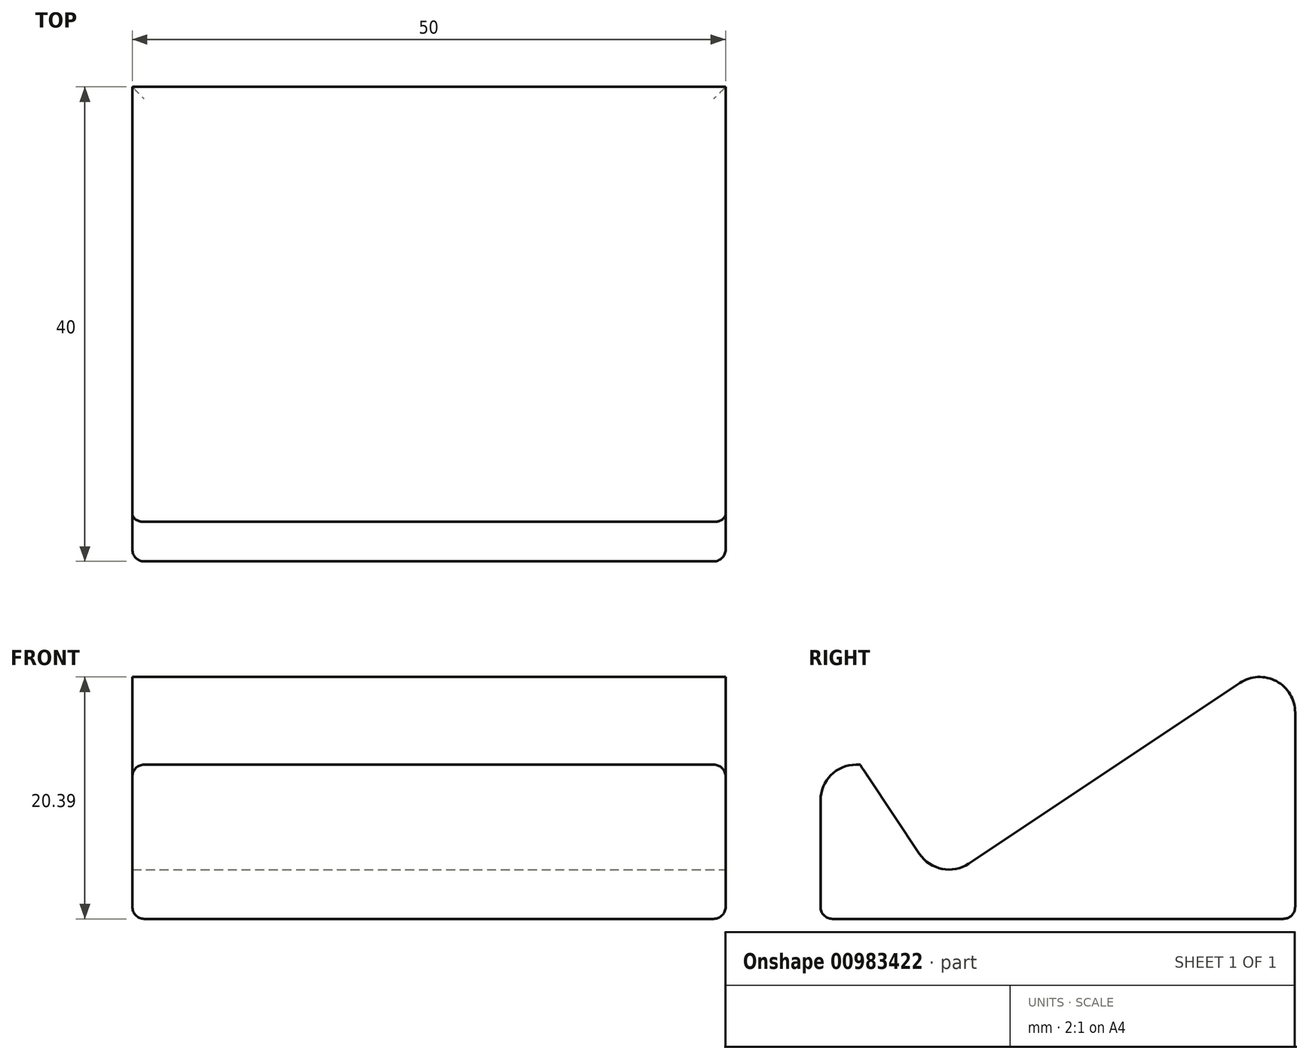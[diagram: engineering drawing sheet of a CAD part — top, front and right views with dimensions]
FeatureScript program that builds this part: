
annotation { "Feature Type Name" : "Feature", "Feature Type Description" : "" }
export const myFeature = defineFeature(function(context is Context, id is Id, definition is map)
    precondition{}
    {
        {
            var Q0;
            Q0=qCreatedBy(makeId("Top.planeOp"),FACE);
            var sketch = newSketch(context, id + "F0", { "sketchPlane" : qUnion([Q0])});
            skLineSegment(sketch, "E0.bottom", {"start": v(25, -20) * mm, "end": v(-25, -20) * mm});
            skLineSegment(sketch, "E0.top", {"start": v(25, 20) * mm, "end": v(-25, 20) * mm});
            skLineSegment(sketch, "E0.left", {"start": v(25, -20) * mm, "end": v(25, 20) * mm});
            skLineSegment(sketch, "E0.right", {"start": v(-25, -20) * mm, "end": v(-25, 20) * mm});
            skPoint(sketch, "E0.middle", {"position": v(0, 0) * mm});
            skSolve(sketch);
        }
        {
            var Q0;
            Q0=makeQuery(id+"F0.imprint","IMPRINT",FACE,{"disambiguationData":[TD([[makeQuery(id+"F0.imprint","IMPRINT",EDGE,{"derivedFrom":sQuery(id+"F0.wireOp",EDGE,"E0.bottom")}),-1.0]])]});
            extrude(context, id + "F1", {"entities" : qUnion([Q0]), "depth" : 3 * mm, "offsetDistance" : 25 * mm});
        }
        {
            var Q0;
            Q0=makeQuery(id+"F1.opExtrude","CAP_FACE",FACE,{"disambiguationData":[OSD([sQuery(id+"F0.wireOp",EDGE,"E0.bottom"),sQuery(id+"F0.wireOp",EDGE,"E0.top"),sQuery(id+"F0.wireOp",EDGE,"E0.left"),sQuery(id+"F0.wireOp",EDGE,"E0.right")])],"isStart":false});
            var sketch = newSketch(context, id + "F2", { "sketchPlane" : qUnion([Q0])});
            skLineSegment(sketch, "E1.bottom", {"start": v(-25, -20) * mm, "end": v(25, -20) * mm});
            skLineSegment(sketch, "E1.top", {"start": v(-25, -10) * mm, "end": v(25, -10) * mm});
            skLineSegment(sketch, "E1.left", {"start": v(-25, -20) * mm, "end": v(-25, -10) * mm});
            skLineSegment(sketch, "E1.right", {"start": v(25, -20) * mm, "end": v(25, -10) * mm});
            skSolve(sketch);
        }
        {
            var Q0;
            {var subQ0=sQuery(id+"F2.wireOp",EDGE,"E1.top");Q0=makeQuery(id+"F2.imprint","IMPRINT",FACE,{"disambiguationData":[TD([[makeQuery(id+"F2.imprint","IMPRINT",EDGE,{"derivedFrom":subQ0}),1.0]])]});}
            extrude(context, id + "F3", {"entities" : qUnion([Q0]), "operationType" : NewBodyOperationType.ADD, "depth" : 20 * mm, "offsetDistance" : 25 * mm});
        }
        {
            var Q0;
            {var subQ0=sQuery(id+"F0.wireOp",EDGE,"E0.left");Q0=makeQuery(id+"F3.boolean.opBoolean","MERGE",FACE,{"derivedFrom":[makeQuery(id+"F1.opExtrude","SWEPT_FACE",FACE,{"disambiguationData":[OSD([subQ0])]}),makeQuery(id+"F3.opExtrude","SWEPT_FACE",FACE,{"disambiguationData":[OSD([subQ0])]})]});}
            var sketch = newSketch(context, id + "F4", { "sketchPlane" : qUnion([Q0])});
            skLineSegment(sketch, "E2", {"start": v(-10, 3) * mm, "end": v(20, 23) * mm});
            skSolve(sketch);
        }
        {
            var Q0;
            Q0=makeQuery(id+"F4.imprint","IMPRINT",FACE,{"disambiguationData":[TD([[makeQuery(id+"F4.imprint","IMPRINT",EDGE,{"derivedFrom":sQuery(id+"F4.wireOp",EDGE,"E2")}),1.0]])]});
            extrude(context, id + "F5", {"entities" : qUnion([Q0]), "operationType" : NewBodyOperationType.REMOVE, "endBound" : BoundingType.UP_TO_NEXT, "oppositeDirection" : true, "depth" : 25 * mm, "offsetDistance" : 25 * mm});
        }
        {
            var Q0;
            Q0=makeQuery(id+"F1.opExtrude","CAP_FACE",FACE,{"disambiguationData":[OSD([sQuery(id+"F0.wireOp",EDGE,"E0.bottom"),sQuery(id+"F0.wireOp",EDGE,"E0.top"),sQuery(id+"F0.wireOp",EDGE,"E0.left"),sQuery(id+"F0.wireOp",EDGE,"E0.right")])],"isStart":false});
            var sketch = newSketch(context, id + "F6", { "sketchPlane" : qUnion([Q0])});
            skSolve(sketch);
        }
        {
            var Q0;
            Q0=makeQuery(id+"F6.imprint","IMPRINT",FACE,{"disambiguationData":[TD([[makeQuery(id+"F6.imprint","IMPRINT",EDGE,{"derivedFrom":makeQuery(id+"F1.opExtrude","CAP_EDGE",EDGE,{"disambiguationData":[OSD([sQuery(id+"F0.wireOp",EDGE,"E0.bottom")])],"isStart":false})}),-1.0]])]});
            extrude(context, id + "F7", {"entities" : qUnion([Q0]), "operationType" : NewBodyOperationType.ADD, "depth" : 10 * mm, "offsetDistance" : 25 * mm});
        }
        {
            var Q0;
            {var subQ0=sQuery(id+"F0.wireOp",EDGE,"E0.left");Q0=makeQuery(id+"F7.boolean.opBoolean","MERGE",FACE,{"derivedFrom":[makeQuery(id+"F3.boolean.opBoolean","MERGE",FACE,{"derivedFrom":[makeQuery(id+"F1.opExtrude","SWEPT_FACE",FACE,{"disambiguationData":[OSD([subQ0])]}),makeQuery(id+"F3.opExtrude","SWEPT_FACE",FACE,{"disambiguationData":[OSD([subQ0])]})]}),makeQuery(id+"F7.opExtrude","SWEPT_FACE",FACE,{"disambiguationData":[OSD([subQ0])]})]});}
            var sketch = newSketch(context, id + "F8", { "sketchPlane" : qUnion([Q0])});
            skLineSegment(sketch, "E3", {"start": v(-10, 3) * mm, "end": v(-16.67, 13) * mm});
            skSolve(sketch);
        }
        {
            var Q0;
            {var subQ0=sQuery(id+"F8.wireOp",EDGE,"E3");Q0=makeQuery(id+"F8.imprint","IMPRINT",FACE,{"disambiguationData":[TD([[makeQuery(id+"F8.imprint","IMPRINT",EDGE,{"derivedFrom":subQ0}),-1.0]])]});}
            extrude(context, id + "F9", {"entities" : qUnion([Q0]), "operationType" : NewBodyOperationType.REMOVE, "endBound" : BoundingType.UP_TO_NEXT, "oppositeDirection" : true, "depth" : 25 * mm, "offsetDistance" : 25 * mm});
        }
        {
            var Q0;
            {var subQ0=sQuery(id+"F2.wireOp",EDGE,"E1.left");var subQ1=sQuery(id+"F2.wireOp",EDGE,"E1.top");var subQ2=sQuery(id+"F0.wireOp",EDGE,"E0.right");Q0=makeQuery(id+"F9.boolean.opBoolean","MERGE",EDGE,{"derivedFrom":[makeQuery(id+"F7.boolean.opBoolean","MERGE",EDGE,{"derivedFrom":[makeQuery(id+"F5.boolean.opBoolean","MERGE",EDGE,{"derivedFrom":[makeQuery(id+"F3.opExtrude","CAP_EDGE",EDGE,{"disambiguationData":[OSD([subQ1])],"isStart":true})],"fromTools":[makeQuery(id+"F5.opExtrude","SWEPT_EDGE",EDGE,{"disambiguationData":[OSD([subQ2,subQ1,subQ0])]})]}),makeQuery(id+"F7.opExtrude","CAP_EDGE",EDGE,{"disambiguationData":[OSD([subQ2,subQ1,subQ0])],"isStart":true})]})],"fromTools":[makeQuery(id+"F9.opExtrude","SWEPT_EDGE",EDGE,{"disambiguationData":[OSD([sQuery(id+"F0.wireOp",EDGE,"E0.left"),subQ2,subQ1,subQ0,sQuery(id+"F2.wireOp",EDGE,"E1.right"),sQuery(id+"F4.wireOp",EDGE,"E2"),sQuery(id+"F8.wireOp",EDGE,"E3")])]})]});}
            var Q1;
            Q1=makeQuery(id+"F9.boolean.opBoolean","COPY",EDGE,{"derivedFrom":makeQuery(id+"F9.opExtrude","SWEPT_EDGE",EDGE,{"disambiguationData":[OSD([sQuery(id+"F0.wireOp",EDGE,"E0.left"),sQuery(id+"F8.wireOp",EDGE,"E3")])]})});
            var Q2;
            Q2=makeQuery(id+"F7.opExtrude","CAP_EDGE",EDGE,{"disambiguationData":[OSD([sQuery(id+"F0.wireOp",EDGE,"E0.bottom")])],"isStart":false});
            var Q3;
            {var subQ0=sQuery(id+"F0.wireOp",EDGE,"E0.top");Q3=makeQuery(id+"F5.boolean.opBoolean","MERGE",EDGE,{"derivedFrom":[makeQuery(id+"F3.opExtrude","CAP_EDGE",EDGE,{"disambiguationData":[OSD([subQ0])],"isStart":false})],"fromTools":[makeQuery(id+"F5.opExtrude","SWEPT_EDGE",EDGE,{"disambiguationData":[OSD([subQ0,sQuery(id+"F0.wireOp",EDGE,"E0.left"),sQuery(id+"F4.wireOp",EDGE,"E2")])]})]});}
            fillet(context, id + "F10", {"entities" : qUnion([Q0, Q1, Q2, Q3]), "radius" : 3 * mm, "tangentPropagation" : true, "allowEdgeOverflow" : false});
        }
        {
            var Q0;
            Q0=makeQuery(id+"F5.boolean.opBoolean","COPY",EDGE,{"derivedFrom":makeQuery(id+"F5.opExtrude","CAP_EDGE",EDGE,{"disambiguationData":[OSD([sQuery(id+"F4.wireOp",EDGE,"E2")])],"isStart":true})});
            var Q1;
            {var subQ0=sQuery(id+"F0.wireOp",EDGE,"E0.right");Q1=makeQuery(id+"F5.boolean.opBoolean","COPY",EDGE,{"derivedFrom":makeQuery(id+"F5.opExtrude","TWEAK_EDGE",EDGE,{"derivedFrom":[makeQuery(id+"F3.boolean.opBoolean","MERGE",FACE,{"derivedFrom":[makeQuery(id+"F1.opExtrude","SWEPT_FACE",FACE,{"disambiguationData":[OSD([subQ0])]}),makeQuery(id+"F3.opExtrude","SWEPT_FACE",FACE,{"disambiguationData":[OSD([subQ0])]})]}),makeQuery(id+"F4.imprint","IMPRINT",EDGE,{"derivedFrom":sQuery(id+"F4.wireOp",EDGE,"E2")})]})});}
            var Q2;
            {var subQ0=sQuery(id+"F0.wireOp",EDGE,"E0.right");var subQ1=sQuery(id+"F0.wireOp",EDGE,"E0.bottom");Q2=makeQuery(id+"F7.boolean.opBoolean","MERGE",EDGE,{"derivedFrom":[makeQuery(id+"F1.opExtrude","SWEPT_EDGE",EDGE,{"disambiguationData":[OSD([subQ1,subQ0])]}),makeQuery(id+"F7.opExtrude","SWEPT_EDGE",EDGE,{"disambiguationData":[OSD([subQ1,subQ0])]})]});}
            var Q3;
            {var subQ0=sQuery(id+"F0.wireOp",EDGE,"E0.left");var subQ1=sQuery(id+"F0.wireOp",EDGE,"E0.bottom");Q3=makeQuery(id+"F7.boolean.opBoolean","MERGE",EDGE,{"derivedFrom":[makeQuery(id+"F1.opExtrude","SWEPT_EDGE",EDGE,{"disambiguationData":[OSD([subQ1,subQ0])]}),makeQuery(id+"F7.opExtrude","SWEPT_EDGE",EDGE,{"disambiguationData":[OSD([subQ1,subQ0])]})]});}
            var Q4;
            Q4=makeQuery(id+"F1.opExtrude","CAP_EDGE",EDGE,{"disambiguationData":[OSD([sQuery(id+"F0.wireOp",EDGE,"E0.left")])],"isStart":true});
            var Q5;
            Q5=makeQuery(id+"F1.opExtrude","CAP_EDGE",EDGE,{"disambiguationData":[OSD([sQuery(id+"F0.wireOp",EDGE,"E0.top")])],"isStart":true});
            var Q6;
            Q6=makeQuery(id+"F1.opExtrude","CAP_EDGE",EDGE,{"disambiguationData":[OSD([sQuery(id+"F0.wireOp",EDGE,"E0.right")])],"isStart":true});
            var Q7;
            Q7=makeQuery(id+"F1.opExtrude","CAP_EDGE",EDGE,{"disambiguationData":[OSD([sQuery(id+"F0.wireOp",EDGE,"E0.bottom")])],"isStart":true});
            fillet(context, id + "F11", {"entities" : qUnion([Q0, Q1, Q2, Q3, Q4, Q5, Q6, Q7]), "radius" : 1 * mm, "tangentPropagation" : true, "allowEdgeOverflow" : false});
        }
    });
